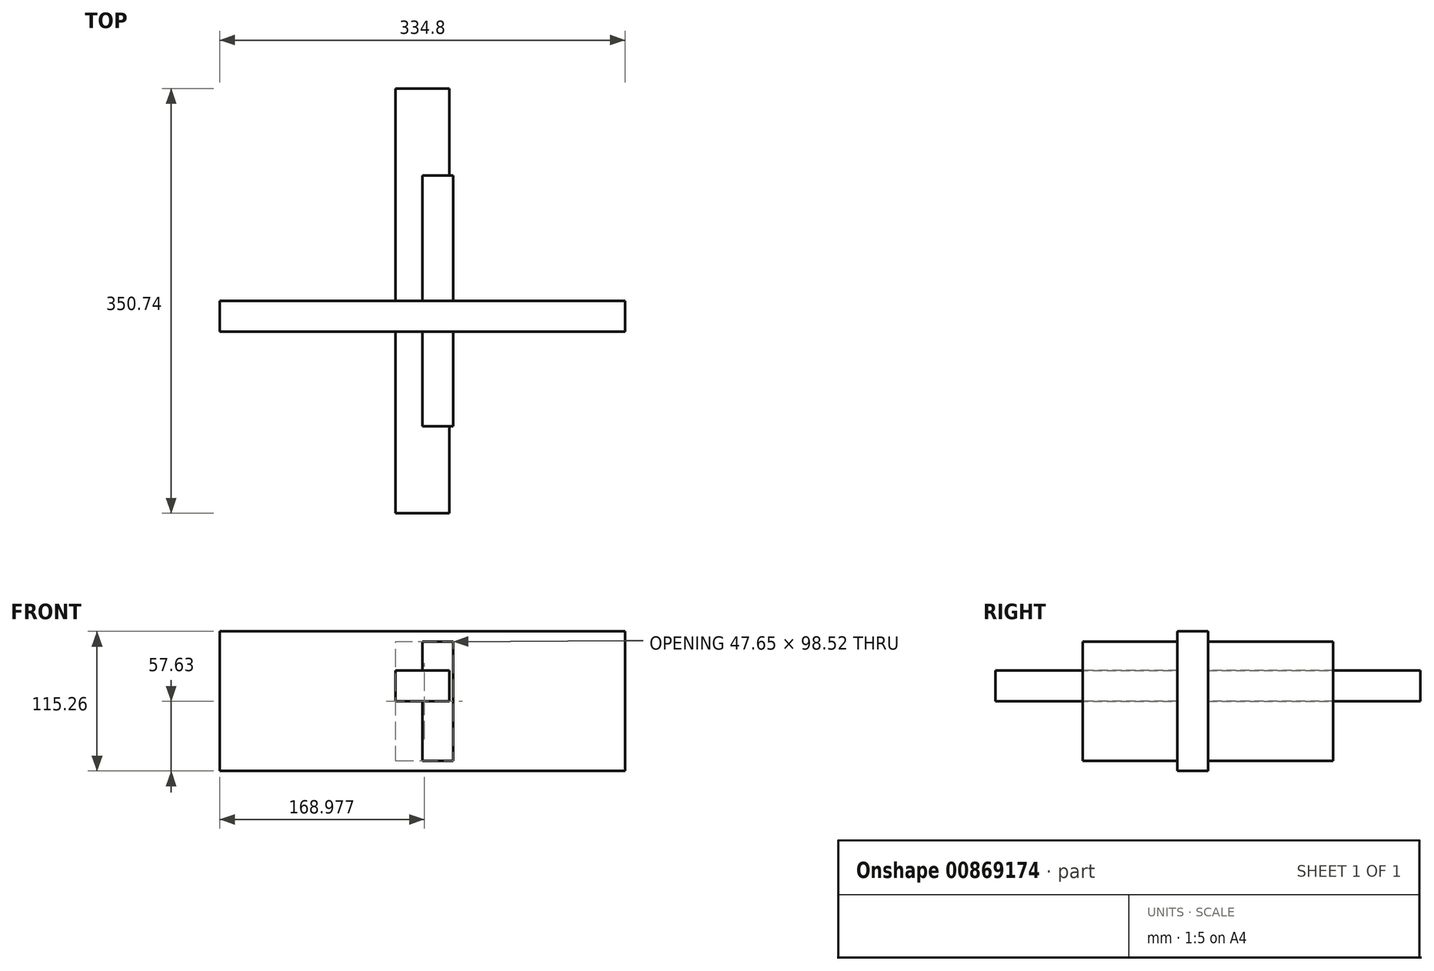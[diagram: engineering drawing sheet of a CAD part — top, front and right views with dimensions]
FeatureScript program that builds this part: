
annotation { "Feature Type Name" : "Feature", "Feature Type Description" : "" }
export const myFeature = defineFeature(function(context is Context, id is Id, definition is map)
    precondition{}
    {
        {
            var Q0;
            Q0=qCreatedBy(makeId("Right.planeOp"),FACE);
            var sketch = newSketch(context, id + "F0", { "sketchPlane" : qUnion([Q0])});
            skLineSegment(sketch, "E0.bottom", {"start": v(103.4, -49.26) * mm, "end": v(-103.4, -49.26) * mm});
            skLineSegment(sketch, "E0.top", {"start": v(103.4, 49.26) * mm, "end": v(-103.4, 49.26) * mm});
            skLineSegment(sketch, "E0.left", {"start": v(103.4, -49.26) * mm, "end": v(103.4, 49.26) * mm});
            skLineSegment(sketch, "E0.right", {"start": v(-103.4, -49.26) * mm, "end": v(-103.4, 49.26) * mm});
            skPoint(sketch, "E0.middle", {"position": v(0, 0) * mm});
            skSolve(sketch);
        }
        {
            var Q0;
            Q0=qCreatedBy(makeId("Front.planeOp"),FACE);
            var sketch = newSketch(context, id + "F1", { "sketchPlane" : qUnion([Q0])});
            skLineSegment(sketch, "E1.bottom", {"start": v(167.4, -57.63) * mm, "end": v(-167.4, -57.63) * mm});
            skLineSegment(sketch, "E1.top", {"start": v(167.4, 57.63) * mm, "end": v(-167.4, 57.63) * mm});
            skLineSegment(sketch, "E1.left", {"start": v(167.4, -57.63) * mm, "end": v(167.4, 57.63) * mm});
            skLineSegment(sketch, "E1.right", {"start": v(-167.4, -57.63) * mm, "end": v(-167.4, 57.63) * mm});
            skPoint(sketch, "E1.middle", {"position": v(0, 0) * mm});
            skSolve(sketch);
        }
        {
            var Q0;
            Q0=qCreatedBy(makeId("Top.planeOp"),FACE);
            var sketch = newSketch(context, id + "F2", { "sketchPlane" : qUnion([Q0])});
            skLineSegment(sketch, "E2.bottom", {"start": v(22.25, -175.37) * mm, "end": v(-22.25, -175.37) * mm});
            skLineSegment(sketch, "E2.top", {"start": v(22.25, 175.37) * mm, "end": v(-22.25, 175.37) * mm});
            skLineSegment(sketch, "E2.left", {"start": v(22.25, -175.37) * mm, "end": v(22.25, 175.37) * mm});
            skLineSegment(sketch, "E2.right", {"start": v(-22.25, -175.37) * mm, "end": v(-22.25, 175.37) * mm});
            skPoint(sketch, "E2.middle", {"position": v(0, 0) * mm});
            skSolve(sketch);
        }
        {
            var Q0;
            Q0 = qSketchRegion(id + "F0", true);
            extrude(context, id + "F3", {"entities" : qUnion([Q0]), "depth" : 25.4 * mm, "offsetDistance" : 25.4 * mm});
        }
        {
            var Q0;
            Q0 = qSketchRegion(id + "F1", true);
            extrude(context, id + "F4", {"entities" : qUnion([Q0]), "operationType" : NewBodyOperationType.ADD, "depth" : 25.4 * mm, "offsetDistance" : 25.4 * mm});
        }
        {
            var Q0;
            Q0 = qSketchRegion(id + "F2", true);
            extrude(context, id + "F5", {"entities" : qUnion([Q0]), "operationType" : NewBodyOperationType.ADD, "depth" : 25.4 * mm, "offsetDistance" : 25.4 * mm});
        }
    });
